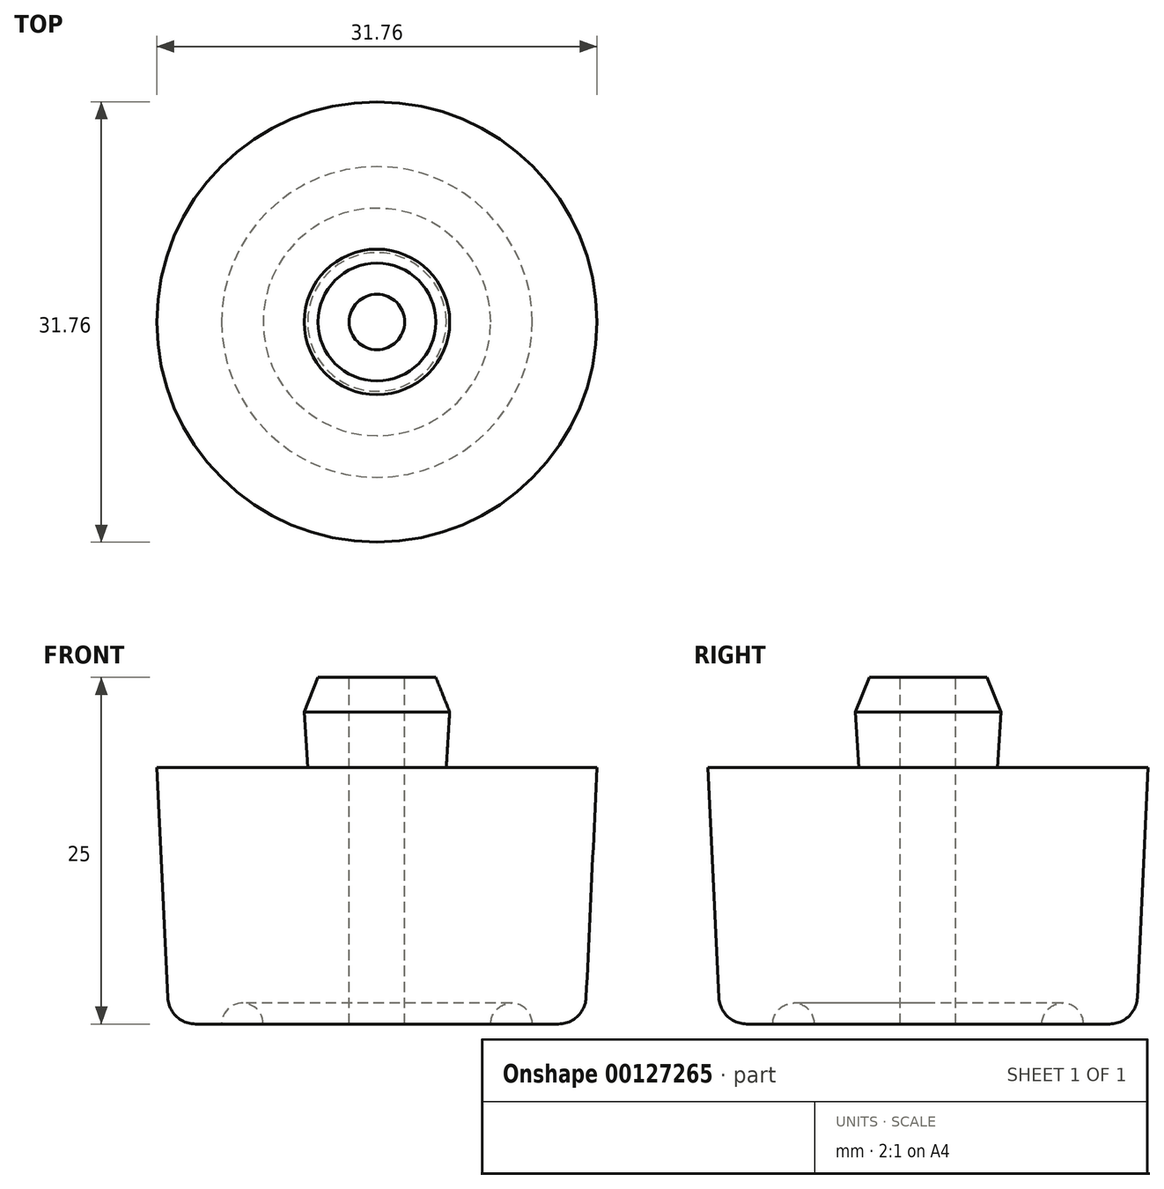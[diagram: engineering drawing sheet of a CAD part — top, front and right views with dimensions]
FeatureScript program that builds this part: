
annotation { "Feature Type Name" : "Feature", "Feature Type Description" : "" }
export const myFeature = defineFeature(function(context is Context, id is Id, definition is map)
    precondition{}
    {
        {
            var Q0;
            Q0=qCreatedBy(makeId("Top.planeOp"),FACE);
            var sketch = newSketch(context, id + "F0", { "sketchPlane" : qUnion([Q0])});
            skCircle(sketch, "E0", {"center": v(0, 0) * mm, "radius": 15 * mm});
            skSolve(sketch);
        }
        {
            var Q0;
            Q0=qCreatedBy(makeId("Top.planeOp"),FACE);
            cPlane(context, id + "F1", {"entities" : qUnion([Q0]), "cplaneType" : CPlaneType.OFFSET, "offset" : 18.5 * mm, "width" : 150 * mm, "height" : 150 * mm});
        }
        {
            var Q0;
            Q0=qCreatedBy(id+"F1.planeOp",FACE);
            var sketch = newSketch(context, id + "F2", { "sketchPlane" : qUnion([Q0])});
            skCircle(sketch, "E1", {"center": v(0, 0) * mm, "radius": 15.88 * mm});
            skSolve(sketch);
        }
        {
            var Q0;
            Q0=makeQuery(id+"F0.imprint","IMPRINT",FACE,{"disambiguationData":[TD([[makeQuery(id+"F0.imprint","IMPRINT",EDGE,{"derivedFrom":sQuery(id+"F0.wireOp",EDGE,"E0")}),1.0]])]});
            var Q1;
            Q1=makeQuery(id+"F2.imprint","IMPRINT",FACE,{"disambiguationData":[TD([[makeQuery(id+"F2.imprint","IMPRINT",EDGE,{"derivedFrom":sQuery(id+"F2.wireOp",EDGE,"E1")}),1.0]])]});
            loft(context, id + "F3", {"sheetProfilesArray" : [{ "sheetProfileEntities" : qUnion([Q0]) }, { "sheetProfileEntities" : qUnion([Q1]) }]});
        }
        {
            var Q0;
            Q0=makeQuery(id+"F3.opLoft","CAP_FACE",FACE,{"disambiguationData":[OSD([makeQuery(id+"F2.imprint","IMPRINT",FACE,{"disambiguationData":[TD([[makeQuery(id+"F2.imprint","IMPRINT",EDGE,{"derivedFrom":sQuery(id+"F2.wireOp",EDGE,"E1")}),1.0]])]})])],"isStart":true});
            var sketch = newSketch(context, id + "F4", { "sketchPlane" : qUnion([Q0])});
            skCircle(sketch, "E2", {"center": v(0, 0) * mm, "radius": 5 * mm});
            skSolve(sketch);
        }
        {
            var Q0;
            Q0=qCreatedBy(makeId("Top.planeOp"),FACE);
            cPlane(context, id + "F5", {"entities" : qUnion([Q0]), "cplaneType" : CPlaneType.OFFSET, "offset" : 22.5 * mm, "width" : 150 * mm, "height" : 150 * mm});
        }
        {
            var Q0;
            Q0=qCreatedBy(id+"F5.planeOp",FACE);
            var sketch = newSketch(context, id + "F6", { "sketchPlane" : qUnion([Q0])});
            skCircle(sketch, "E3", {"center": v(0, 0) * mm, "radius": 5.25 * mm});
            skSolve(sketch);
        }
        {
            var Q1;
            Q1=makeQuery(id+"F4.imprint","IMPRINT",FACE,{"disambiguationData":[TD([[makeQuery(id+"F4.imprint","IMPRINT",EDGE,{"derivedFrom":sQuery(id+"F4.wireOp",EDGE,"E2")}),1.0]])]});
            var Q2;
            Q2=makeQuery(id+"F6.imprint","IMPRINT",FACE,{"disambiguationData":[TD([[makeQuery(id+"F6.imprint","IMPRINT",EDGE,{"derivedFrom":sQuery(id+"F6.wireOp",EDGE,"E3")}),1.0]])]});
            loft(context, id + "F7", {"operationType" : NewBodyOperationType.ADD, "sheetProfilesArray" : [{ "sheetProfileEntities" : qUnion([Q1]) }, { "sheetProfileEntities" : qUnion([Q2]) }]});
        }
        {
            var Q0;
            Q0=qCreatedBy(makeId("Top.planeOp"),FACE);
            cPlane(context, id + "F8", {"entities" : qUnion([Q0]), "cplaneType" : CPlaneType.OFFSET, "offset" : (22.5 + 2.5) * mm, "width" : 150 * mm, "height" : 150 * mm});
        }
        {
            var Q0;
            Q0=qCreatedBy(id+"F8.planeOp",FACE);
            var sketch = newSketch(context, id + "F9", { "sketchPlane" : qUnion([Q0])});
            skCircle(sketch, "E4", {"center": v(0, 0) * mm, "radius": 4.25 * mm});
            skSolve(sketch);
        }
        {
            var Q1;
            Q1=makeQuery(id+"F7.opLoft","CAP_FACE",FACE,{"disambiguationData":[OSD([makeQuery(id+"F6.imprint","IMPRINT",FACE,{"disambiguationData":[TD([[makeQuery(id+"F6.imprint","IMPRINT",EDGE,{"derivedFrom":sQuery(id+"F6.wireOp",EDGE,"E3")}),1.0]])]})])],"isStart":true});
            var Q2;
            Q2=makeQuery(id+"F9.imprint","IMPRINT",FACE,{"disambiguationData":[TD([[makeQuery(id+"F9.imprint","IMPRINT",EDGE,{"derivedFrom":sQuery(id+"F9.wireOp",EDGE,"E4")}),1.0]])]});
            loft(context, id + "F10", {"operationType" : NewBodyOperationType.ADD, "sheetProfilesArray" : [{ "sheetProfileEntities" : qUnion([Q1]) }, { "sheetProfileEntities" : qUnion([Q2]) }]});
        }
        {
            var Q0;
            Q0=makeQuery(id+"F10.opLoft","CAP_FACE",FACE,{"disambiguationData":[OSD([makeQuery(id+"F9.imprint","IMPRINT",FACE,{"disambiguationData":[TD([[makeQuery(id+"F9.imprint","IMPRINT",EDGE,{"derivedFrom":sQuery(id+"F9.wireOp",EDGE,"E4")}),1.0]])]})])],"isStart":true});
            var sketch = newSketch(context, id + "F11", { "sketchPlane" : qUnion([Q0])});
            skCircle(sketch, "E5", {"center": v(0, 0) * mm, "radius": 2 * mm});
            skSolve(sketch);
        }
        {
            var Q0;
            Q0 = qSketchRegion(id + "F11", true);
            extrude(context, id + "F12", {"entities" : qUnion([Q0]), "operationType" : NewBodyOperationType.REMOVE, "endBound" : BoundingType.THROUGH_ALL, "oppositeDirection" : true, "depth" : 25 * mm});
        }
        {
            var Q0;
            Q0=qCreatedBy(makeId("Front.planeOp"),FACE);
            var sketch = newSketch(context, id + "F13", { "sketchPlane" : qUnion([Q0])});
            skCircle(sketch, "E6", {"center": v(-9.7, 0) * mm, "radius": 1.5 * mm});
            skLineSegment(sketch, "E7", {"start": v(0, 28.04) * mm, "end": v(0, -12.9) * mm, "construction": true});
            skSolve(sketch);
        }
        {
            var Q0;
            Q0=makeQuery(id+"F13.imprint","IMPRINT",FACE,{"disambiguationData":[TD([[makeQuery(id+"F13.imprint","IMPRINT",EDGE,{"derivedFrom":sQuery(id+"F13.wireOp",EDGE,"E6")}),1.0]])]});
            var Q1;
            Q1=sQuery(id+"F13.wireOp",EDGE,"E7");
            revolve(context, id + "F14", {"operationType" : NewBodyOperationType.REMOVE, "entities" : qUnion([Q0]), "axis" : qUnion([Q1]), "revolveType" : RevolveType.FULL, "oppositeDirection" : true});
        }
        {
            var Q0;
            Q0=makeQuery(id+"F3.opLoft","MID_CAP_EDGE",EDGE,{"disambiguationData":[OSD([sQuery(id+"F0.wireOp",EDGE,"E0")])],"capPos":0.0});
            fillet(context, id + "F15", {"entities" : qUnion([Q0]), "radius" : 2 * mm, "tangentPropagation" : true, "allowEdgeOverflow" : false});
        }
    });
